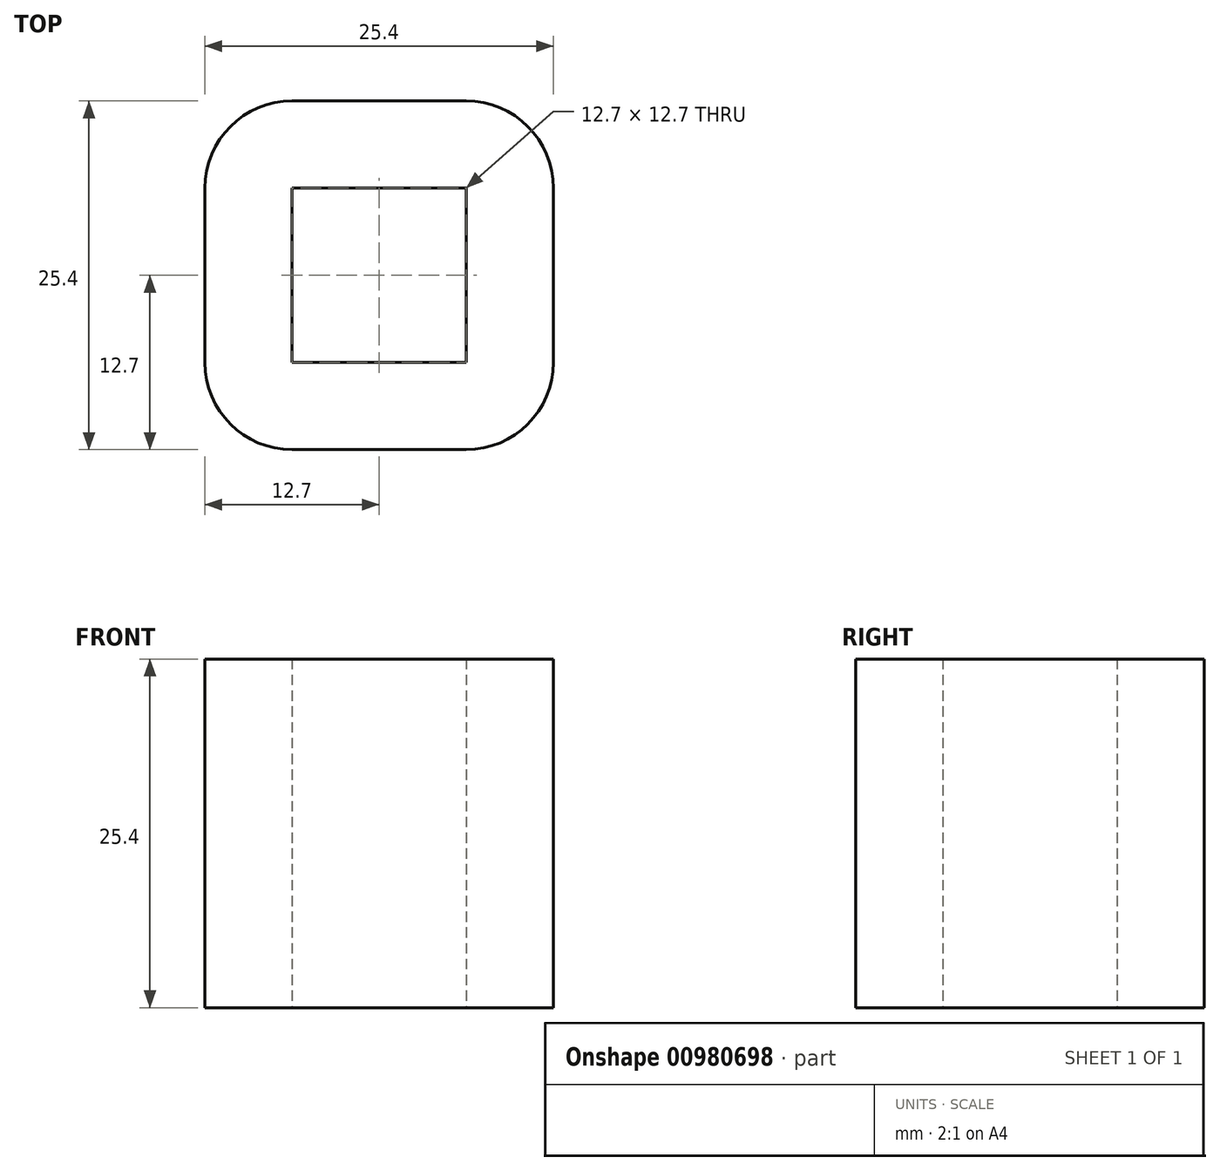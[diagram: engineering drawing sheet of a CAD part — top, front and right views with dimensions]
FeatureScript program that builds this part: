
annotation { "Feature Type Name" : "Feature", "Feature Type Description" : "" }
export const myFeature = defineFeature(function(context is Context, id is Id, definition is map)
    precondition{}
    {
        {
            var Q0;
            Q0=qCreatedBy(makeId("Top.planeOp"),FACE);
            var sketch = newSketch(context, id + "F0", { "sketchPlane" : qUnion([Q0])});
            skLineSegment(sketch, "E0", {"start": v(0, 0) * mm, "end": v(0, 12.7) * mm, "construction": true});
            skLineSegment(sketch, "E1.bottom", {"start": v(-6.35, 12.7) * mm, "end": v(6.35, 12.7) * mm});
            skLineSegment(sketch, "E1.top", {"start": v(-6.35, -12.7) * mm, "end": v(6.35, -12.7) * mm});
            skLineSegment(sketch, "E1.left", {"start": v(-12.7, 6.35) * mm, "end": v(-12.7, -6.35) * mm});
            skLineSegment(sketch, "E1.right", {"start": v(12.7, 6.35) * mm, "end": v(12.7, -6.35) * mm});
            skPoint(sketch, "E1.middle", {"position": v(0, 0) * mm});
            skPoint(sketch, "E2.visualSharp", {"position": v(-12.7, 12.7) * mm});
            skArc(sketch, "E2.filletArc", {"start": v(-6.35, 12.7) * mm, "mid": v(-10.84, 10.84) * mm, "end": v(-12.7, 6.35) * mm});
            skPoint(sketch, "E3.visualSharp", {"position": v(-12.7, -12.7) * mm});
            skArc(sketch, "E3.filletArc", {"start": v(-12.7, -6.35) * mm, "mid": v(-10.84, -10.84) * mm, "end": v(-6.35, -12.7) * mm});
            skPoint(sketch, "E4.visualSharp", {"position": v(12.7, -12.7) * mm});
            skArc(sketch, "E4.filletArc", {"start": v(6.35, -12.7) * mm, "mid": v(10.84, -10.84) * mm, "end": v(12.7, -6.35) * mm});
            skPoint(sketch, "E5.visualSharp", {"position": v(12.7, 12.7) * mm});
            skArc(sketch, "E5.filletArc", {"start": v(12.7, 6.35) * mm, "mid": v(10.84, 10.84) * mm, "end": v(6.35, 12.7) * mm});
            skLineSegment(sketch, "E6.bottom", {"start": v(6.35, -6.35) * mm, "end": v(-6.35, -6.35) * mm});
            skLineSegment(sketch, "E6.top", {"start": v(6.35, 6.35) * mm, "end": v(-6.35, 6.35) * mm});
            skLineSegment(sketch, "E6.left", {"start": v(6.35, -6.35) * mm, "end": v(6.35, 6.35) * mm});
            skLineSegment(sketch, "E6.right", {"start": v(-6.35, -6.35) * mm, "end": v(-6.35, 6.35) * mm});
            skSolve(sketch);
        }
        {
            var Q0;
            Q0=makeQuery(id+"F0.imprint","IMPRINT",FACE,{"disambiguationData":[TD([[makeQuery(id+"F0.imprint","IMPRINT",EDGE,{"derivedFrom":sQuery(id+"F0.wireOp",EDGE,"E1.bottom")}),-1.0]])]});
            extrude(context, id + "F1", {"entities" : qUnion([Q0]), "endBound" : BoundingType.SYMMETRIC, "depth" : 25.4 * mm, "offsetDistance" : 25.4 * mm});
        }
    });
